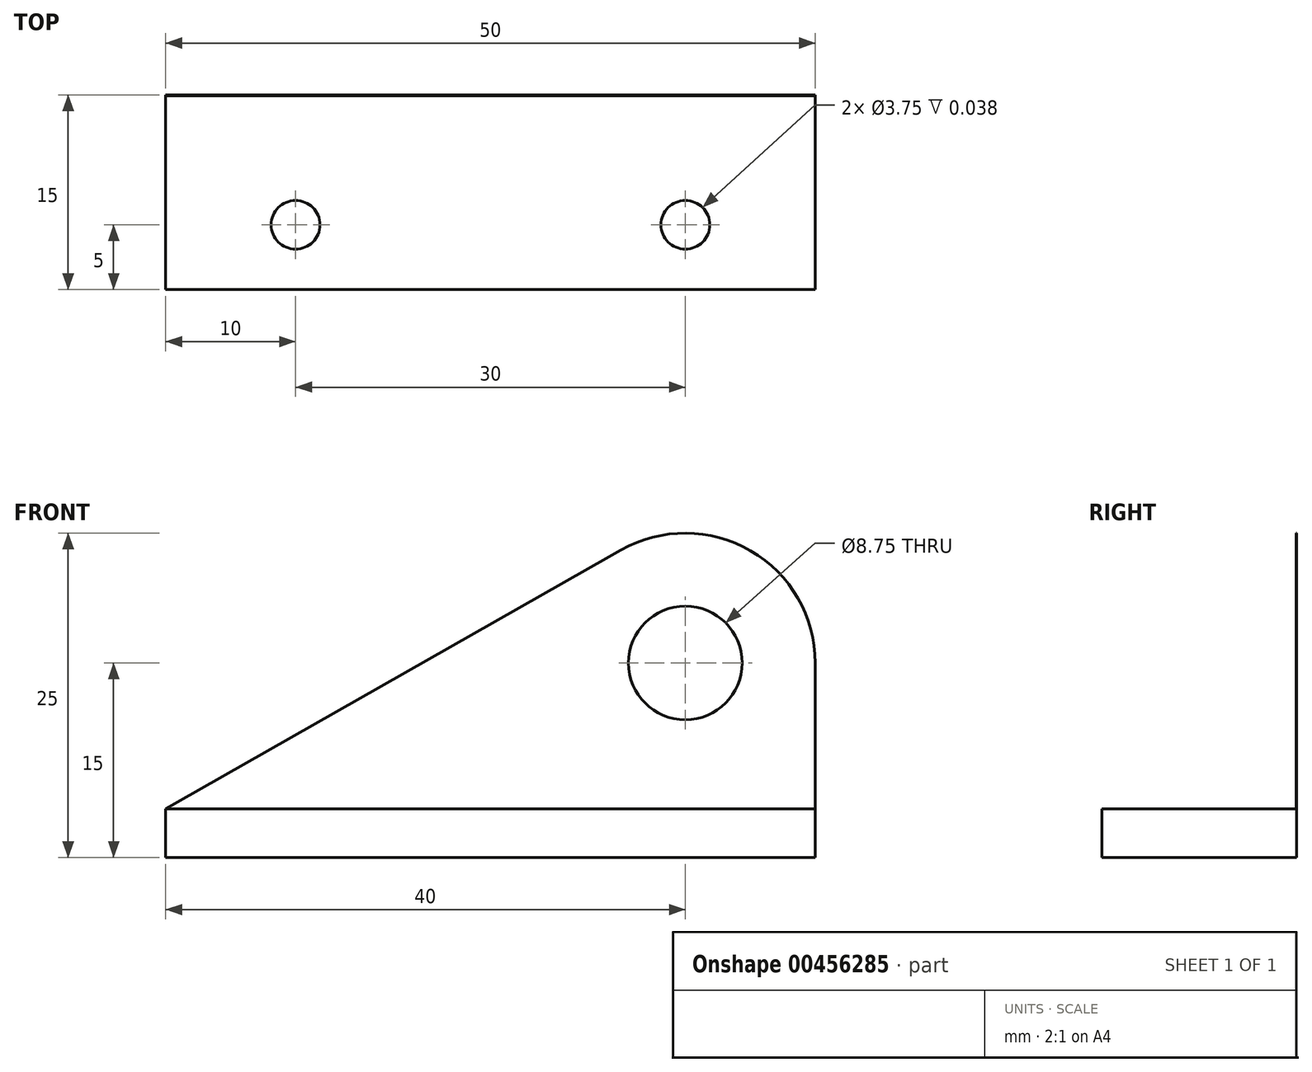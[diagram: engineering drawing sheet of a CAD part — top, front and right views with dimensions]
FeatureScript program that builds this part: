
annotation { "Feature Type Name" : "Feature", "Feature Type Description" : "" }
export const myFeature = defineFeature(function(context is Context, id is Id, definition is map)
    precondition{}
    {
        {
            var Q0;
            Q0=qCreatedBy(makeId("Front.planeOp"),FACE);
            var sketch = newSketch(context, id + "F0", { "sketchPlane" : qUnion([Q0])});
            skLineSegment(sketch, "E0.bottom", {"start": v(0, 0) * mm, "end": v(-50, 0) * mm});
            skLineSegment(sketch, "E0.top", {"start": v(0, 3.75) * mm, "end": v(-50, 3.75) * mm});
            skLineSegment(sketch, "E0.left", {"start": v(0, 0) * mm, "end": v(0, 3.75) * mm});
            skLineSegment(sketch, "E0.right", {"start": v(-50, 0) * mm, "end": v(-50, 3.75) * mm});
            skArc(sketch, "E1", {"start": v(0, 15) * mm, "mid": v(-4.97, 23.64) * mm, "end": v(-14.94, 23.7) * mm});
            skCircle(sketch, "E2", {"center": v(-10, 15) * mm, "radius": 4.38 * mm});
            skLineSegment(sketch, "E3", {"start": v(-50, 3.75) * mm, "end": v(-14.94, 23.7) * mm});
            skLineSegment(sketch, "E4", {"start": v(0, 15) * mm, "end": v(0, 3.75) * mm});
            skSolve(sketch);
        }
        {
            var Q0;
            Q0=makeQuery(id+"F0.imprint","IMPRINT",FACE,{"disambiguationData":[TD([[makeQuery(id+"F0.imprint","IMPRINT",EDGE,{"derivedFrom":sQuery(id+"F0.wireOp",EDGE,"E0.bottom")}),-1.0]])]});
            var Q1;
            Q1=makeQuery(id+"F0.imprint","IMPRINT",FACE,{"disambiguationData":[TD([[makeQuery(id+"F0.imprint","IMPRINT",EDGE,{"derivedFrom":sQuery(id+"F0.wireOp",EDGE,"E0.top")}),-1.0]])]});
            extrude(context, id + "F1", {"entities" : qUnion([Q0, Q1]), "depth" : 1 / 20 * mm, "offsetDistance" : 25 * mm});
        }
        {
            var Q0;
            Q0=makeQuery(id+"F0.imprint","IMPRINT",FACE,{"disambiguationData":[TD([[makeQuery(id+"F0.imprint","IMPRINT",EDGE,{"derivedFrom":sQuery(id+"F0.wireOp",EDGE,"E0.bottom")}),-1.0]])]});
            extrude(context, id + "F2", {"entities" : qUnion([Q0]), "operationType" : NewBodyOperationType.ADD, "depth" : 15 * mm, "offsetDistance" : 25 * mm});
        }
        {
            var Q0;
            Q0=makeQuery(id+"F2.opExtrude","SWEPT_FACE",FACE,{"disambiguationData":[OSD([sQuery(id+"F0.wireOp",EDGE,"E0.top")])]});
            var sketch = newSketch(context, id + "F3", { "sketchPlane" : qUnion([Q0])});
            skCircle(sketch, "E5", {"center": v(-40, -10) * mm, "radius": 1.88 * mm});
            skCircle(sketch, "E6", {"center": v(-10, -10) * mm, "radius": 1.88 * mm});
            skSolve(sketch);
        }
        {
            var Q0;
            Q0 = qSketchRegion(id + "F3", true);
            extrude(context, id + "F4", {"entities" : qUnion([Q0]), "operationType" : NewBodyOperationType.REMOVE, "oppositeDirection" : true, "depth" : 3 / 80 * mm, "offsetDistance" : 25 * mm});
        }
    });
